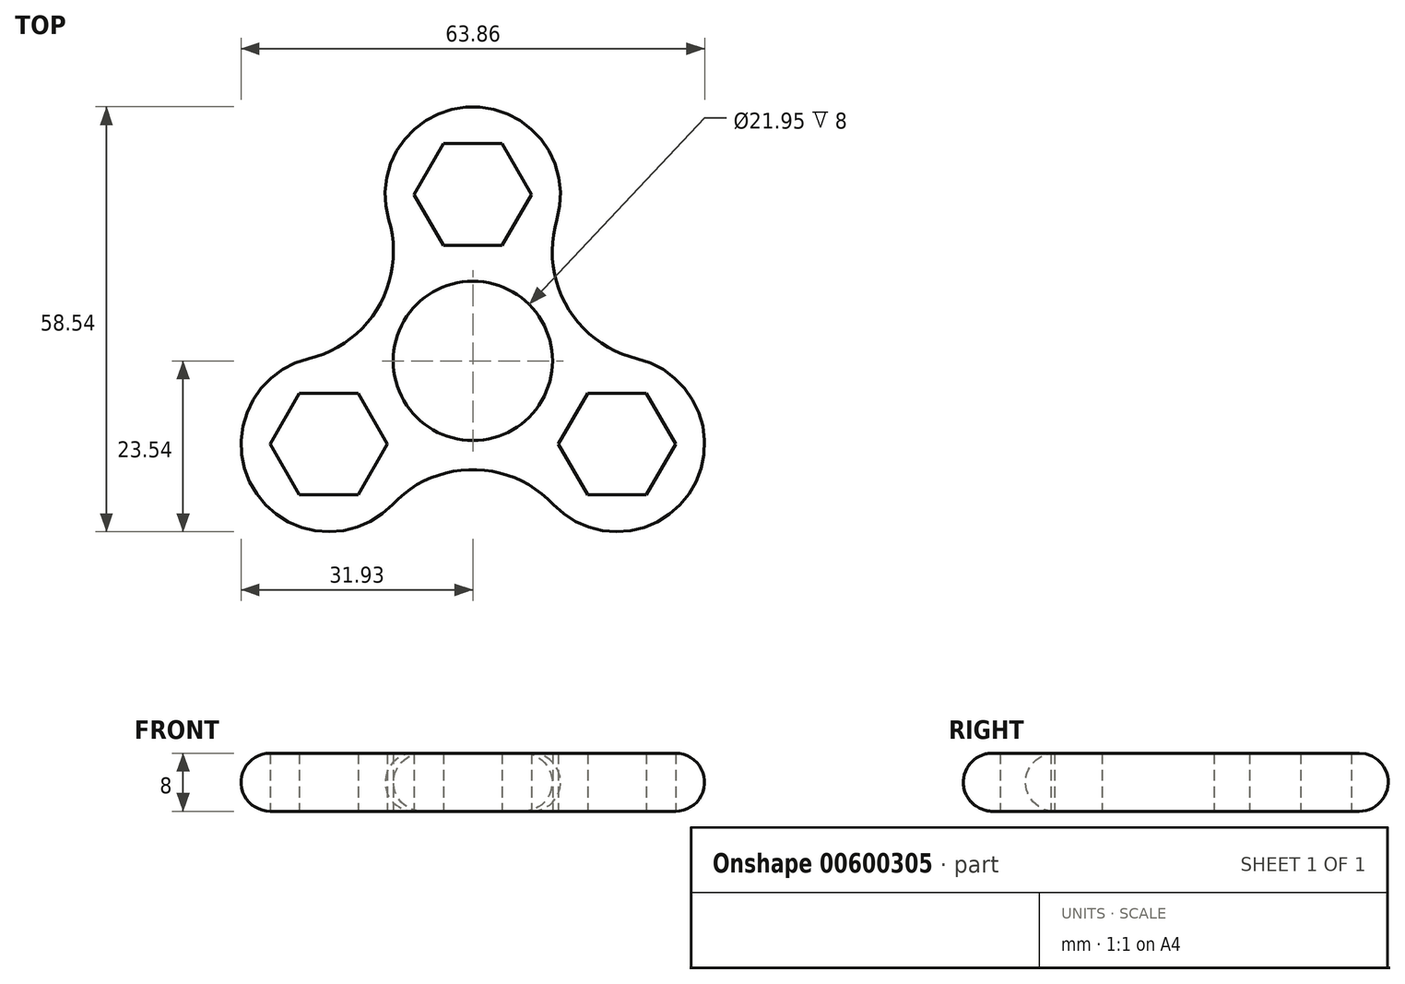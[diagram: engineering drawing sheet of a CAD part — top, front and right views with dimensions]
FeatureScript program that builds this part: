
annotation { "Feature Type Name" : "Feature", "Feature Type Description" : "" }
export const myFeature = defineFeature(function(context is Context, id is Id, definition is map)
    precondition{}
    {
        {
            var Q0;
            Q0=qCreatedBy(makeId("Top.planeOp"),FACE);
            var sketch = newSketch(context, id + "F0", { "sketchPlane" : qUnion([Q0])});
            skCircle(sketch, "E0", {"center": v(0, 0) * mm, "radius": 35 * mm, "construction": true});
            skLineSegment(sketch, "E1", {"start": v(0, 22.92) * mm, "end": v(0, 0) * mm, "construction": true});
            skLineSegment(sketch, "E2", {"start": v(0, 0) * mm, "end": v(-19.85, -11.46) * mm, "construction": true});
            skLineSegment(sketch, "E3", {"start": v(0, 0) * mm, "end": v(19.85, -11.46) * mm, "construction": true});
            skCircle(sketch, "E4.cCircle", {"center": v(0, 22.92) * mm, "radius": 7 * mm, "construction": true});
            skLineSegment(sketch, "E4.0", {"start": v(8.08, 22.92) * mm, "end": v(4.04, 15.92) * mm});
            skLineSegment(sketch, "E4.1", {"start": v(4.04, 15.92) * mm, "end": v(-4.04, 15.92) * mm});
            skLineSegment(sketch, "E4.2", {"start": v(-4.04, 15.92) * mm, "end": v(-8.08, 22.92) * mm});
            skLineSegment(sketch, "E4.3", {"start": v(-8.08, 22.92) * mm, "end": v(-4.04, 29.92) * mm});
            skLineSegment(sketch, "E4.4", {"start": v(-4.04, 29.92) * mm, "end": v(4.04, 29.92) * mm});
            skLineSegment(sketch, "E4.5", {"start": v(4.04, 29.92) * mm, "end": v(8.08, 22.92) * mm});
            skPoint(sketch, "E4.0.midPoint", {"position": v(6.06, 19.42) * mm});
            skArc(sketch, "E5.cCircle", {"start": v(11.57, 19.45) * mm, "mid": v(0, 35) * mm, "end": v(-11.57, 19.45) * mm});
            skCircle(sketch, "E6", {"center": v(0, 0) * mm, "radius": 10.97 * mm});
            skCircle(sketch, "E7.cCircle", {"center": v(19.85, -11.46) * mm, "radius": 7 * mm, "construction": true});
            skLineSegment(sketch, "E7.0", {"start": v(27.93, -11.46) * mm, "end": v(23.89, -18.46) * mm});
            skLineSegment(sketch, "E7.1", {"start": v(23.89, -18.46) * mm, "end": v(15.8, -18.46) * mm});
            skLineSegment(sketch, "E7.2", {"start": v(15.8, -18.46) * mm, "end": v(11.76, -11.46) * mm});
            skLineSegment(sketch, "E7.3", {"start": v(11.76, -11.46) * mm, "end": v(15.8, -4.46) * mm});
            skLineSegment(sketch, "E7.4", {"start": v(15.8, -4.46) * mm, "end": v(23.89, -4.46) * mm});
            skLineSegment(sketch, "E7.5", {"start": v(23.89, -4.46) * mm, "end": v(27.93, -11.46) * mm});
            skPoint(sketch, "E7.0.midPoint", {"position": v(25.9, -14.96) * mm});
            skArc(sketch, "E8.cCircle", {"start": v(11.05, -19.75) * mm, "mid": v(30.31, -17.5) * mm, "end": v(22.63, 0.3) * mm});
            skCircle(sketch, "E9.cCircle", {"center": v(-19.85, -11.46) * mm, "radius": 7 * mm, "construction": true});
            skLineSegment(sketch, "E9.0", {"start": v(-11.76, -11.46) * mm, "end": v(-15.8, -18.46) * mm});
            skLineSegment(sketch, "E9.1", {"start": v(-15.8, -18.46) * mm, "end": v(-23.89, -18.46) * mm});
            skLineSegment(sketch, "E9.2", {"start": v(-23.89, -18.46) * mm, "end": v(-27.93, -11.46) * mm});
            skLineSegment(sketch, "E9.3", {"start": v(-27.93, -11.46) * mm, "end": v(-23.89, -4.46) * mm});
            skLineSegment(sketch, "E9.4", {"start": v(-23.89, -4.46) * mm, "end": v(-15.8, -4.46) * mm});
            skLineSegment(sketch, "E9.5", {"start": v(-15.8, -4.46) * mm, "end": v(-11.76, -11.46) * mm});
            skPoint(sketch, "E9.0.midPoint", {"position": v(-13.78, -14.96) * mm});
            skArc(sketch, "E10", {"start": v(-22.63, 0.3) * mm, "mid": v(-30.31, -17.5) * mm, "end": v(-11.05, -19.75) * mm});
            skArc(sketch, "E11", {"start": v(-22.63, 0.3) * mm, "mid": v(-12.97, 7.49) * mm, "end": v(-11.57, 19.45) * mm});
            skArc(sketch, "E12", {"start": v(11.05, -19.75) * mm, "mid": v(0, -14.97) * mm, "end": v(-11.05, -19.75) * mm});
            skArc(sketch, "E13", {"start": v(11.57, 19.45) * mm, "mid": v(12.97, 7.49) * mm, "end": v(22.63, 0.3) * mm});
            skSolve(sketch);
        }
        {
            var Q0;
            Q0=qSketchRegion(id+"F0",true);
            extrude(context, id + "F1", {"entities" : qUnion([Q0]), "endBound" : BoundingType.SYMMETRIC, "depth" : 8 * mm, "offsetDistance" : 25 * mm});
        }
        {
            var Q0;
            Q0=makeQuery(id+"F1.opExtrude","CAP_EDGE",EDGE,{"disambiguationData":[OSD([sQuery(id+"F0.wireOp",EDGE,"E11")])],"isStart":false});
            var Q1;
            Q1=makeQuery(id+"F1.opExtrude","CAP_EDGE",EDGE,{"disambiguationData":[OSD([sQuery(id+"F0.wireOp",EDGE,"E11")])],"isStart":true});
            fillet(context, id + "F2", {"entities" : qUnion([Q0, Q1]), "radius" : 4 * mm, "tangentPropagation" : true, "allowEdgeOverflow" : false});
        }
    });
